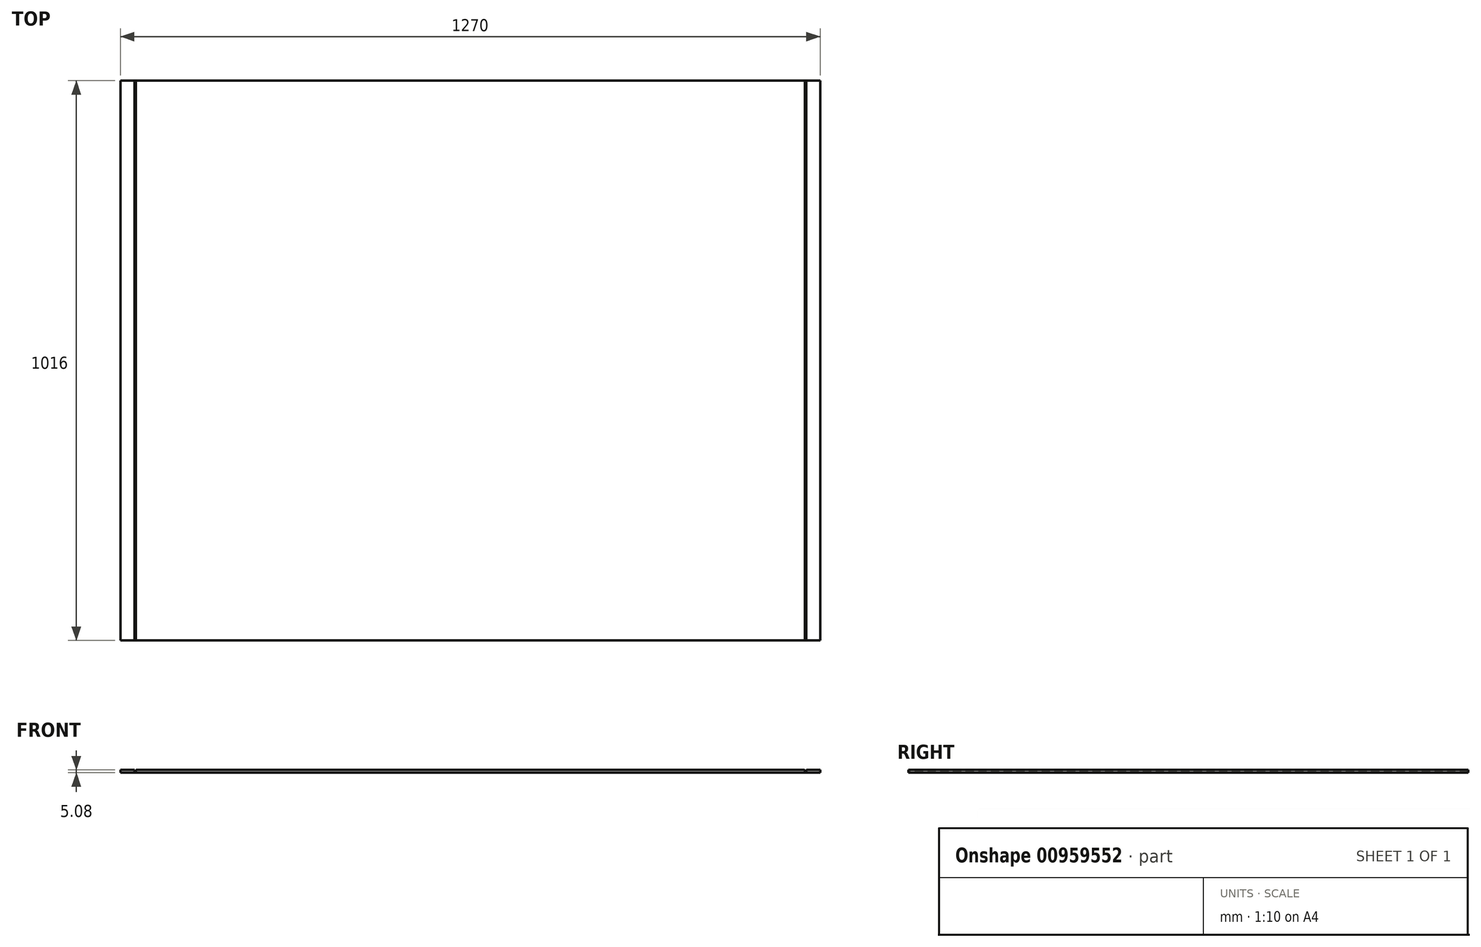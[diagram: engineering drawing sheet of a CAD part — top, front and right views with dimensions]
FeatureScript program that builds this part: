
annotation { "Feature Type Name" : "Feature", "Feature Type Description" : "" }
export const myFeature = defineFeature(function(context is Context, id is Id, definition is map)
    precondition{}
    {
        {
            var Q0;
            Q0=qCreatedBy(makeId("Top.planeOp"),FACE);
            var sketch = newSketch(context, id + "F0", { "sketchPlane" : qUnion([Q0])});
            skLineSegment(sketch, "E0.bottom", {"start": v(-117.46, 915.72) * mm, "end": v(1152.54, 915.72) * mm});
            skLineSegment(sketch, "E0.top", {"start": v(-117.46, -100.28) * mm, "end": v(1152.54, -100.28) * mm});
            skLineSegment(sketch, "E0.left", {"start": v(-117.46, 915.72) * mm, "end": v(-117.46, -100.28) * mm});
            skLineSegment(sketch, "E0.right", {"start": v(1152.54, 915.72) * mm, "end": v(1152.54, -100.28) * mm});
            skSolve(sketch);
        }
        {
            var Q0;
            Q0=makeQuery(id+"F0.imprint","IMPRINT",FACE,{"disambiguationData":[TD([[makeQuery(id+"F0.imprint","IMPRINT",EDGE,{"derivedFrom":sQuery(id+"F0.wireOp",EDGE,"E0.bottom")}),-1.0]])]});
            extrude(context, id + "F1", {"entities" : qUnion([Q0]), "depth" : 5.08 * mm, "offsetDistance" : 25.4 * mm});
        }
        {
            var Q0;
            Q0=makeQuery(id+"F1.opExtrude","CAP_FACE",FACE,{"disambiguationData":[OSD([sQuery(id+"F0.wireOp",EDGE,"E0.bottom"),sQuery(id+"F0.wireOp",EDGE,"E0.top"),sQuery(id+"F0.wireOp",EDGE,"E0.left"),sQuery(id+"F0.wireOp",EDGE,"E0.right")])],"isStart":false});
            var sketch = newSketch(context, id + "F2", { "sketchPlane" : qUnion([Q0])});
            skLineSegment(sketch, "E1", {"start": v(-92.06, 915.72) * mm, "end": v(-92.06, -100.28) * mm});
            skLineSegment(sketch, "E2", {"start": v(-89.52, 915.72) * mm, "end": v(-89.52, -100.28) * mm});
            skLineSegment(sketch, "E3", {"start": v(1127.14, 915.72) * mm, "end": v(1127.14, -100.28) * mm});
            skLineSegment(sketch, "E4", {"start": v(1124.6, 915.72) * mm, "end": v(1124.6, -100.28) * mm});
            skSolve(sketch);
        }
        {
            var Q0;
            {var subQ0=sQuery(id+"F2.wireOp",EDGE,"E3");Q0=makeQuery(id+"F2.imprint","IMPRINT",FACE,{"disambiguationData":[TD([[makeQuery(id+"F2.imprint","IMPRINT",EDGE,{"derivedFrom":subQ0}),-1.0]])]});}
            var Q1;
            {var subQ0=sQuery(id+"F2.wireOp",EDGE,"E1");Q1=makeQuery(id+"F2.imprint","IMPRINT",FACE,{"disambiguationData":[TD([[makeQuery(id+"F2.imprint","IMPRINT",EDGE,{"derivedFrom":subQ0}),1.0]])]});}
            extrude(context, id + "F3", {"entities" : qUnion([Q0, Q1]), "operationType" : NewBodyOperationType.REMOVE, "oppositeDirection" : true, "depth" : 2.54 * mm, "offsetDistance" : 25.4 * mm});
        }
        {
            var Q0;
            Q0=makeQuery(id+"F3.boolean.opBoolean","COPY",EDGE,{"derivedFrom":makeQuery(id+"F3.opExtrude","CAP_EDGE",EDGE,{"disambiguationData":[OSD([sQuery(id+"F2.wireOp",EDGE,"E3")])],"isStart":true})});
            var Q1;
            Q1=makeQuery(id+"F3.boolean.opBoolean","COPY",EDGE,{"derivedFrom":makeQuery(id+"F3.opExtrude","CAP_EDGE",EDGE,{"disambiguationData":[OSD([sQuery(id+"F2.wireOp",EDGE,"E4")])],"isStart":true})});
            fillet(context, id + "F4", {"entities" : qUnion([Q0, Q1]), "radius" : 1.27 * mm, "tangentPropagation" : true, "allowEdgeOverflow" : false});
        }
        {
            var Q0;
            Q0=makeQuery(id+"F3.boolean.opBoolean","COPY",EDGE,{"derivedFrom":makeQuery(id+"F3.opExtrude","CAP_EDGE",EDGE,{"disambiguationData":[OSD([sQuery(id+"F2.wireOp",EDGE,"E3")])],"isStart":false})});
            var Q1;
            Q1=makeQuery(id+"F3.boolean.opBoolean","COPY",EDGE,{"derivedFrom":makeQuery(id+"F3.opExtrude","CAP_EDGE",EDGE,{"disambiguationData":[OSD([sQuery(id+"F2.wireOp",EDGE,"E4")])],"isStart":false})});
            fillet(context, id + "F5", {"entities" : qUnion([Q0, Q1]), "radius" : 0.5 * mm, "tangentPropagation" : true, "allowEdgeOverflow" : false});
        }
        {
            var Q0;
            Q0=makeQuery(id+"F3.boolean.opBoolean","COPY",EDGE,{"derivedFrom":makeQuery(id+"F3.opExtrude","CAP_EDGE",EDGE,{"disambiguationData":[OSD([sQuery(id+"F2.wireOp",EDGE,"E2")])],"isStart":true})});
            var Q1;
            Q1=makeQuery(id+"F3.boolean.opBoolean","COPY",EDGE,{"derivedFrom":makeQuery(id+"F3.opExtrude","CAP_EDGE",EDGE,{"disambiguationData":[OSD([sQuery(id+"F2.wireOp",EDGE,"E1")])],"isStart":true})});
            fillet(context, id + "F6", {"entities" : qUnion([Q0, Q1]), "radius" : 1.27 * mm, "tangentPropagation" : true, "allowEdgeOverflow" : false});
        }
        {
            var Q0;
            Q0=makeQuery(id+"F3.boolean.opBoolean","COPY",EDGE,{"derivedFrom":makeQuery(id+"F3.opExtrude","CAP_EDGE",EDGE,{"disambiguationData":[OSD([sQuery(id+"F2.wireOp",EDGE,"E1")])],"isStart":false})});
            var Q1;
            Q1=makeQuery(id+"F3.boolean.opBoolean","COPY",EDGE,{"derivedFrom":makeQuery(id+"F3.opExtrude","CAP_EDGE",EDGE,{"disambiguationData":[OSD([sQuery(id+"F2.wireOp",EDGE,"E2")])],"isStart":false})});
            fillet(context, id + "F7", {"entities" : qUnion([Q0, Q1]), "radius" : 0.5 * mm, "tangentPropagation" : true, "allowEdgeOverflow" : false});
        }
    });
